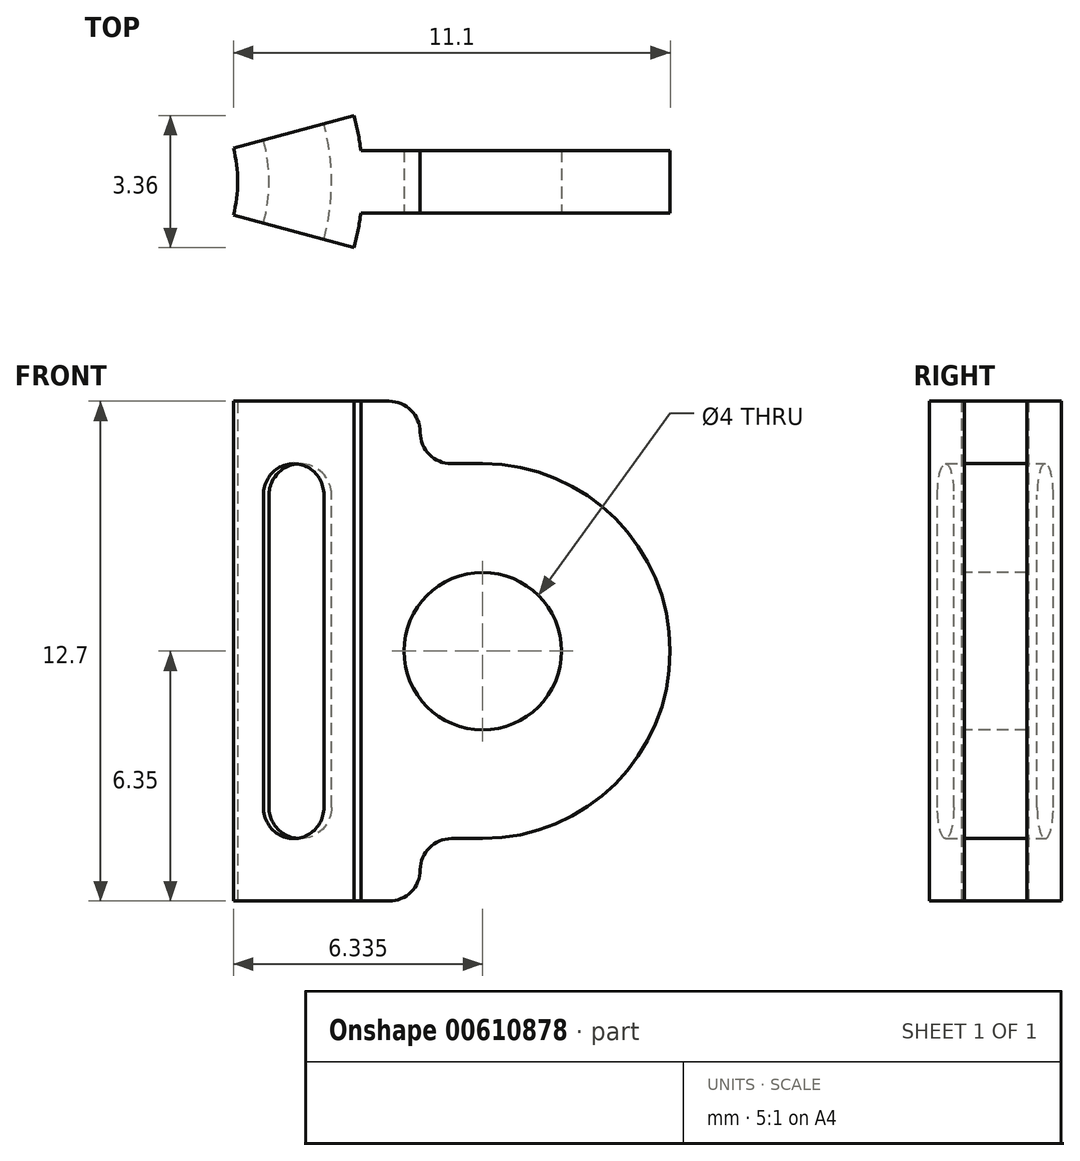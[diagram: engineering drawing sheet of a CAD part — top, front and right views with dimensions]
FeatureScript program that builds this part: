
annotation { "Feature Type Name" : "Feature", "Feature Type Description" : "" }
export const myFeature = defineFeature(function(context is Context, id is Id, definition is map)
    precondition{}
    {
        {
            var Q0;
            Q0=qCreatedBy(makeId("Top.planeOp"),FACE);
            var sketch = newSketch(context, id + "F0", { "sketchPlane" : qUnion([Q0])});
            skCircle(sketch, "E0", {"center": v(0, 0) * mm, "radius": 3.3 * mm});
            skCircle(sketch, "E1", {"center": v(0, 0) * mm, "radius": 6.48 * mm});
            skSolve(sketch);
        }
        {
            var Q0;
            Q0 = qSketchRegion(id + "F0", true);
            extrude(context, id + "F1", {"entities" : qUnion([Q0]), "endBound" : BoundingType.SYMMETRIC, "depth" : 12.7 * mm, "offsetDistance" : 25.4 * mm});
        }
        {
            var Q0;
            Q0=qCreatedBy(makeId("Front.planeOp"),FACE);
            var sketch = newSketch(context, id + "F2", { "sketchPlane" : qUnion([Q0])});
            skLineSegment(sketch, "E2.bottom", {"start": v(-6.35, 6.35) * mm, "end": v(6.35, 6.35) * mm, "construction": true});
            skLineSegment(sketch, "E2.top", {"start": v(-6.35, -6.35) * mm, "end": v(6.35, -6.35) * mm, "construction": true});
            skLineSegment(sketch, "E2.left", {"start": v(-6.35, 6.35) * mm, "end": v(-6.35, -6.35) * mm, "construction": true});
            skLineSegment(sketch, "E3", {"start": v(0, 6.35) * mm, "end": v(0, 0) * mm, "construction": true});
            skLineSegment(sketch, "E4", {"start": v(0, 0) * mm, "end": v(0, -6.35) * mm, "construction": true});
            skLineSegment(sketch, "E5", {"start": v(7.94, 6.35) * mm, "end": v(7.94, 4.76) * mm});
            skLineSegment(sketch, "E6", {"start": v(7.94, 4.76) * mm, "end": v(14.29, 4.76) * mm});
            skLineSegment(sketch, "E7", {"start": v(14.29, 4.76) * mm, "end": v(14.29, 0) * mm});
            skLineSegment(sketch, "E8", {"start": v(14.29, 0) * mm, "end": v(14.29, -4.76) * mm});
            skLineSegment(sketch, "E9", {"start": v(14.29, -4.76) * mm, "end": v(7.94, -4.76) * mm});
            skLineSegment(sketch, "E10", {"start": v(7.94, -4.76) * mm, "end": v(7.94, -6.35) * mm});
            skLineSegment(sketch, "E11", {"start": v(4.76, 6.35) * mm, "end": v(4.76, -6.35) * mm});
            skLineSegment(sketch, "E12", {"start": v(7.94, 6.35) * mm, "end": v(4.76, 6.35) * mm});
            skLineSegment(sketch, "E13", {"start": v(7.94, -6.35) * mm, "end": v(4.76, -6.35) * mm});
            skSolve(sketch);
        }
        {
            var Q0;
            Q0 = qSketchRegion(id + "F2", true);
            extrude(context, id + "F3", {"entities" : qUnion([Q0]), "operationType" : NewBodyOperationType.ADD, "endBound" : BoundingType.SYMMETRIC, "depth" : 1.59 * mm, "offsetDistance" : 25.4 * mm});
        }
        {
            var Q0;
            Q0=makeQuery(id+"F3.opExtrude","SWEPT_EDGE",EDGE,{"disambiguationData":[OSD([sQuery(id+"F2.wireOp",EDGE,"E5"),sQuery(id+"F2.wireOp",EDGE,"E12")])]});
            var Q1;
            Q1=makeQuery(id+"F3.opExtrude","SWEPT_EDGE",EDGE,{"disambiguationData":[OSD([sQuery(id+"F2.wireOp",EDGE,"E5"),sQuery(id+"F2.wireOp",EDGE,"E6")])]});
            var Q2;
            Q2=makeQuery(id+"F3.opExtrude","SWEPT_EDGE",EDGE,{"disambiguationData":[OSD([sQuery(id+"F2.wireOp",EDGE,"E10"),sQuery(id+"F2.wireOp",EDGE,"E13")])]});
            var Q3;
            Q3=makeQuery(id+"F3.opExtrude","SWEPT_EDGE",EDGE,{"disambiguationData":[OSD([sQuery(id+"F2.wireOp",EDGE,"E9"),sQuery(id+"F2.wireOp",EDGE,"E10")])]});
            fillet(context, id + "F4", {"entities" : qUnion([Q0, Q1, Q2, Q3]), "radius" : 0.8 * mm, "tangentPropagation" : true, "allowEdgeOverflow" : false});
        }
        {
            var Q0;
            Q0=makeQuery(id+"F3.opExtrude","SWEPT_EDGE",EDGE,{"disambiguationData":[OSD([sQuery(id+"F2.wireOp",EDGE,"E8"),sQuery(id+"F2.wireOp",EDGE,"E9")])]});
            var Q1;
            Q1=makeQuery(id+"F3.opExtrude","SWEPT_EDGE",EDGE,{"disambiguationData":[OSD([sQuery(id+"F2.wireOp",EDGE,"E6"),sQuery(id+"F2.wireOp",EDGE,"E7")])]});
            fillet(context, id + "F5", {"entities" : qUnion([Q0, Q1]), "radius" : 4.76 * mm, "tangentPropagation" : true, "allowEdgeOverflow" : false});
        }
        {
            var Q0;
            Q0=makeQuery(id+"F3.opExtrude","CAP_FACE",FACE,{"disambiguationData":[OSD([sQuery(id+"F2.wireOp",EDGE,"E5"),sQuery(id+"F2.wireOp",EDGE,"E6"),sQuery(id+"F2.wireOp",EDGE,"E7"),sQuery(id+"F2.wireOp",EDGE,"E8"),sQuery(id+"F2.wireOp",EDGE,"E9"),sQuery(id+"F2.wireOp",EDGE,"E10"),sQuery(id+"F2.wireOp",EDGE,"E11"),sQuery(id+"F2.wireOp",EDGE,"E12"),sQuery(id+"F2.wireOp",EDGE,"E13")])],"isStart":false});
            var sketch = newSketch(context, id + "F6", { "sketchPlane" : qUnion([Q0])});
            skPoint(sketch, "E14", {"position": v(9.53, 0) * mm});
            skSolve(sketch);
        }
        {
            var Q0;
            Q0=sQuery(id+"F6.wireOp",VERTEX,"E14");
            var Q1;
            Q1=makeQuery(id+"F1.opExtrude","SWEPT_BODY",BODY,{"disambiguationData":[OSD([sQuery(id+"F0.wireOp",EDGE,"E0"),sQuery(id+"F0.wireOp",EDGE,"E1")])]});
            hole(context, id + "F7", {"style" : HoleStyle.SIMPLE, "endStyle" : HoleEndStyle.THROUGH, "holeDiameter" : 4 * mm, "majorDiameter" : 6.35 * mm, "isTappedThrough" : true, "tappedDepth" : 12.7 * mm, "tapClearance" : 3, "locations" : qUnion([Q0]), "scope" : qUnion([Q1])});
        }
        {
            var Q0;
            Q0=makeQuery(id+"F1.opExtrude","SWEPT_BODY",BODY,{"disambiguationData":[OSD([sQuery(id+"F0.wireOp",EDGE,"E0"),sQuery(id+"F0.wireOp",EDGE,"E1")])]});
            var Q1;
            Q1=makeQuery(id+"F1.opExtrude","CAP_EDGE",EDGE,{"disambiguationData":[OSD([sQuery(id+"F0.wireOp",EDGE,"E0")])],"isStart":false});
            circularPattern(context, id + "F8", {"operationType" : NewBodyOperationType.ADD, "entities" : qUnion([Q0]), "axis" : qUnion([Q1]), "angle" : 360 * degree, "instanceCount" : 12, "equalSpace" : true});
        }
        {
            var Q0;
            {var subQ0=makeQuery(id+"F3.boolean.opBoolean","MERGE",FACE,{"derivedFrom":[makeQuery(id+"F1.opExtrude","CAP_FACE",FACE,{"disambiguationData":[OSD([sQuery(id+"F0.wireOp",EDGE,"E0"),sQuery(id+"F0.wireOp",EDGE,"E1")])],"isStart":false}),makeQuery(id+"F3.opExtrude","SWEPT_FACE",FACE,{"disambiguationData":[OSD([sQuery(id+"F2.wireOp",EDGE,"E12")])]})]});Q0=makeQuery(id+"F8.boolean.opBoolean","MERGE",FACE,{"derivedFrom":[subQ0,makeQuery(id+"F8.opPattern","COPY",FACE,{"derivedFrom":subQ0,"instanceName":"1"}),makeQuery(id+"F8.opPattern","COPY",FACE,{"derivedFrom":subQ0,"instanceName":"2"}),makeQuery(id+"F8.opPattern","COPY",FACE,{"derivedFrom":subQ0,"instanceName":"3"}),makeQuery(id+"F8.opPattern","COPY",FACE,{"derivedFrom":subQ0,"instanceName":"4"}),makeQuery(id+"F8.opPattern","COPY",FACE,{"derivedFrom":subQ0,"instanceName":"5"}),makeQuery(id+"F8.opPattern","COPY",FACE,{"derivedFrom":subQ0,"instanceName":"6"}),makeQuery(id+"F8.opPattern","COPY",FACE,{"derivedFrom":subQ0,"instanceName":"7"}),makeQuery(id+"F8.opPattern","COPY",FACE,{"derivedFrom":subQ0,"instanceName":"8"}),makeQuery(id+"F8.opPattern","COPY",FACE,{"derivedFrom":subQ0,"instanceName":"9"}),makeQuery(id+"F8.opPattern","COPY",FACE,{"derivedFrom":subQ0,"instanceName":"10"}),makeQuery(id+"F8.opPattern","COPY",FACE,{"derivedFrom":subQ0,"instanceName":"11"})]});}
            var sketch = newSketch(context, id + "F9", { "sketchPlane" : qUnion([Q0])});
            skLineSegment(sketch, "E15", {"start": v(6.26, 1.68) * mm, "end": v(3.19, 0.85) * mm});
            skLineSegment(sketch, "E16", {"start": v(6.26, -1.68) * mm, "end": v(3.19, -0.85) * mm});
            skArc(sketch, "E17", {"start": v(15.33, 4.1) * mm, "mid": v(-15.88, 0) * mm, "end": v(15.33, -4.1) * mm});
            skLineSegment(sketch, "E18", {"start": v(3.19, 0.85) * mm, "end": v(3.19, -0.85) * mm});
            skLineSegment(sketch, "E19", {"start": v(6.26, 1.68) * mm, "end": v(15.33, 4.1) * mm});
            skLineSegment(sketch, "E20", {"start": v(6.26, -1.68) * mm, "end": v(15.33, -4.1) * mm});
            skSolve(sketch);
        }
        {
            var Q0;
            Q0 = qSketchRegion(id + "F9", true);
            extrude(context, id + "F10", {"entities" : qUnion([Q0]), "operationType" : NewBodyOperationType.REMOVE, "endBound" : BoundingType.THROUGH_ALL, "oppositeDirection" : true, "depth" : 25.4 * mm, "offsetDistance" : 25.4 * mm});
        }
        {
            var Q0;
            Q0=qCreatedBy(makeId("Top.planeOp"),FACE);
            var sketch = newSketch(context, id + "F11", { "sketchPlane" : qUnion([Q0])});
            skArc(sketch, "E21", {"start": v(4.72, -1.27) * mm, "mid": v(4.89, 0) * mm, "end": v(4.72, 1.27) * mm, "construction": true});
            skLineSegment(sketch, "E22", {"start": v(4.72, -1.27) * mm, "end": v(3.96, -1.06) * mm});
            skLineSegment(sketch, "E23", {"start": v(4.72, -1.27) * mm, "end": v(5.49, -1.47) * mm});
            skLineSegment(sketch, "E24", {"start": v(4.72, 1.27) * mm, "end": v(5.49, 1.47) * mm});
            skLineSegment(sketch, "E25", {"start": v(4.72, 1.27) * mm, "end": v(3.96, 1.06) * mm});
            skArc(sketch, "E26", {"start": v(5.49, -1.47) * mm, "mid": v(5.68, 0) * mm, "end": v(5.49, 1.47) * mm});
            skArc(sketch, "E27", {"start": v(3.96, -1.06) * mm, "mid": v(4.1, 0) * mm, "end": v(3.96, 1.06) * mm});
            skSolve(sketch);
        }
        {
            var Q0;
            Q0 = qSketchRegion(id + "F11", true);
            extrude(context, id + "F12", {"entities" : qUnion([Q0]), "operationType" : NewBodyOperationType.REMOVE, "endBound" : BoundingType.SYMMETRIC, "oppositeDirection" : true, "depth" : 9.52 * mm, "offsetDistance" : 25.4 * mm});
        }
        {
            var Q0;
            Q0=makeQuery(id+"F12.boolean.opBoolean","COPY",EDGE,{"derivedFrom":makeQuery(id+"F12.opExtrude","CAP_EDGE",EDGE,{"disambiguationData":[OSD([sQuery(id+"F11.wireOp",EDGE,"E26")])],"isStart":false})});
            var Q1;
            Q1=makeQuery(id+"F12.boolean.opBoolean","COPY",EDGE,{"derivedFrom":makeQuery(id+"F12.opExtrude","CAP_EDGE",EDGE,{"disambiguationData":[OSD([sQuery(id+"F11.wireOp",EDGE,"E27")])],"isStart":false})});
            var Q2;
            Q2=makeQuery(id+"F12.boolean.opBoolean","COPY",EDGE,{"derivedFrom":makeQuery(id+"F12.opExtrude","CAP_EDGE",EDGE,{"disambiguationData":[OSD([sQuery(id+"F11.wireOp",EDGE,"E27")])],"isStart":true})});
            var Q3;
            Q3=makeQuery(id+"F12.boolean.opBoolean","COPY",EDGE,{"derivedFrom":makeQuery(id+"F12.opExtrude","CAP_EDGE",EDGE,{"disambiguationData":[OSD([sQuery(id+"F11.wireOp",EDGE,"E26")])],"isStart":true})});
            fillet(context, id + "F13", {"entities" : qUnion([Q0, Q1, Q2, Q3]), "radius" : 0.8 * mm, "tangentPropagation" : true, "allowEdgeOverflow" : false});
        }
    });
